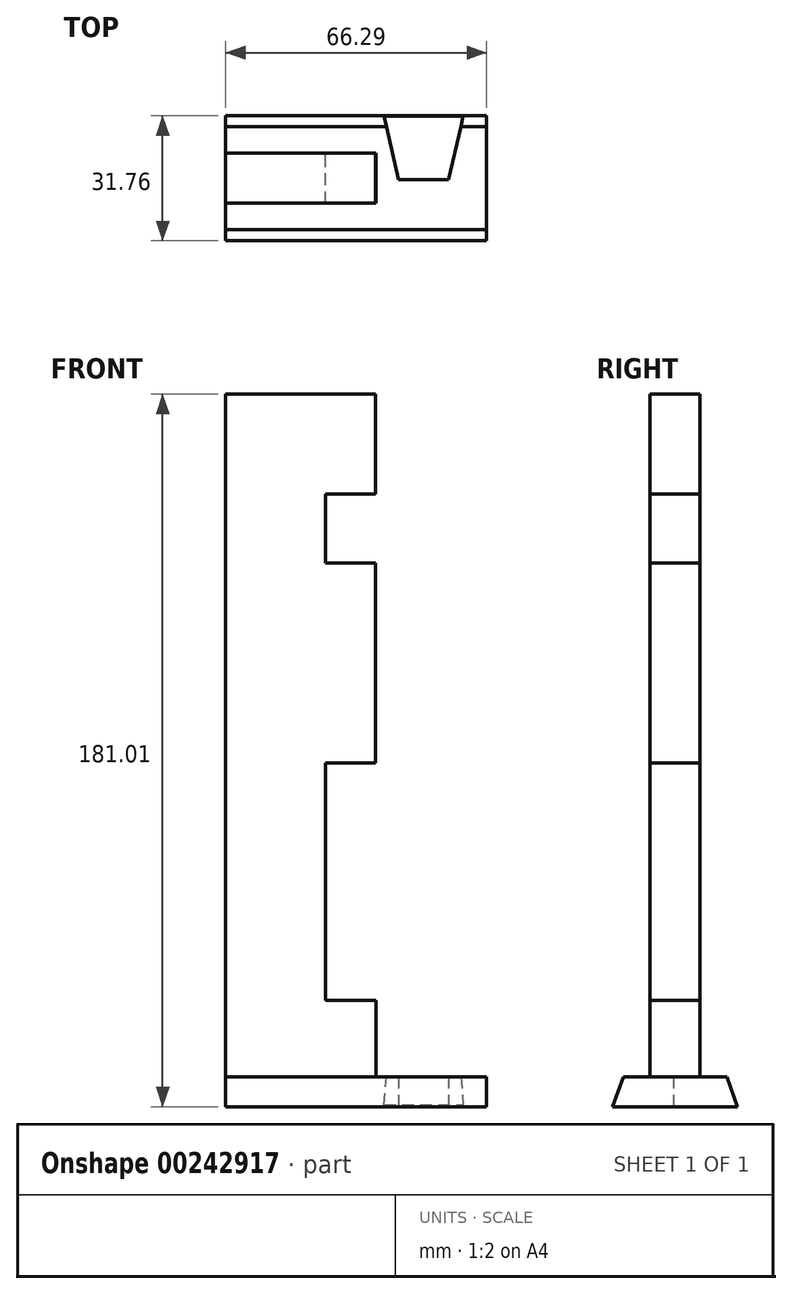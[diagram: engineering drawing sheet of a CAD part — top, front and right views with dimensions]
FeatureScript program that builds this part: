
annotation { "Feature Type Name" : "Feature", "Feature Type Description" : "" }
export const myFeature = defineFeature(function(context is Context, id is Id, definition is map)
    precondition{}
    {
        {
            var Q0;
            Q0=qCreatedBy(makeId("Front.planeOp"),FACE);
            var sketch = newSketch(context, id + "F0", { "sketchPlane" : qUnion([Q0])});
            skLineSegment(sketch, "E0", {"start": v(0, 0) * mm, "end": v(0, 173.39) * mm});
            skLineSegment(sketch, "E1", {"start": v(0, 173.39) * mm, "end": v(38.1, 173.39) * mm});
            skLineSegment(sketch, "E2", {"start": v(38.1, 173.39) * mm, "end": v(38.1, 147.99) * mm});
            skLineSegment(sketch, "E3", {"start": v(38.1, 147.99) * mm, "end": v(25.4, 147.99) * mm});
            skLineSegment(sketch, "E4", {"start": v(25.4, 147.99) * mm, "end": v(25.4, 130.53) * mm});
            skLineSegment(sketch, "E5", {"start": v(25.4, 130.53) * mm, "end": v(38.1, 130.53) * mm});
            skLineSegment(sketch, "E6", {"start": v(38.1, 130.53) * mm, "end": v(38.1, 79.73) * mm});
            skLineSegment(sketch, "E7", {"start": v(38.1, 79.73) * mm, "end": v(25.4, 79.73) * mm});
            skLineSegment(sketch, "E8", {"start": v(25.4, 79.73) * mm, "end": v(25.4, 19.4) * mm});
            skLineSegment(sketch, "E9", {"start": v(25.4, 19.4) * mm, "end": v(38.1, 19.4) * mm});
            skLineSegment(sketch, "E10", {"start": v(38.1, 19.4) * mm, "end": v(38.1, 0) * mm});
            skLineSegment(sketch, "E11", {"start": v(38.1, 0) * mm, "end": v(0, 0) * mm});
            skSolve(sketch);
        }
        {
            var Q0;
            Q0=makeQuery(id+"F0.imprint","IMPRINT",FACE,{"disambiguationData":[TD([[makeQuery(id+"F0.imprint","IMPRINT",EDGE,{"derivedFrom":sQuery(id+"F0.wireOp",EDGE,"E0")}),-1.0]])]});
            extrude(context, id + "F1", {"entities" : qUnion([Q0]), "depth" : 12.7 * mm});
        }
        {
            var Q0;
            Q0=makeQuery(id+"F1.opExtrude","SWEPT_FACE",FACE,{"disambiguationData":[OSD([sQuery(id+"F0.wireOp",EDGE,"E10")])]});
            var sketch = newSketch(context, id + "F2", { "sketchPlane" : qUnion([Q0])});
            skLineSegment(sketch, "E12.bottom", {"start": v(0, 0) * mm, "end": v(-12.7, 0) * mm});
            skLineSegment(sketch, "E12.top", {"start": v(0, -7.62) * mm, "end": v(-12.7, -7.62) * mm});
            skLineSegment(sketch, "E12.left", {"start": v(0, 0) * mm, "end": v(0, -7.62) * mm});
            skLineSegment(sketch, "E12.right", {"start": v(-12.7, 0) * mm, "end": v(-12.7, -7.62) * mm});
            skLineSegment(sketch, "E13", {"start": v(-12.7, -7.62) * mm, "end": v(-9.93, 0) * mm});
            skLineSegment(sketch, "E14", {"start": v(-9.93, 0) * mm, "end": v(-2.77, 0) * mm});
            skLineSegment(sketch, "E15", {"start": v(-2.77, 0) * mm, "end": v(0, -7.62) * mm});
            skSolve(sketch);
        }
        {
            var Q0;
            Q0=makeQuery(id+"F2.imprint","IMPRINT",FACE,{"disambiguationData":[TD([[makeQuery(id+"F2.imprint","IMPRINT",EDGE,{"derivedFrom":sQuery(id+"F2.wireOp",EDGE,"E12.top")}),-1.0]])]});
            extrude(context, id + "F3", {"entities" : qUnion([Q0]), "operationType" : NewBodyOperationType.ADD, "oppositeDirection" : true, "depth" : 38.1 * mm});
        }
        {
            var Q0;
            Q0=makeQuery(id+"F3.boolean.opBoolean","MERGE",FACE,{"derivedFrom":[makeQuery(id+"F1.opExtrude","SWEPT_FACE",FACE,{"disambiguationData":[OSD([sQuery(id+"F0.wireOp",EDGE,"E0")])]}),makeQuery(id+"F3.opExtrude","CAP_FACE",FACE,{"disambiguationData":[OSD([sQuery(id+"F2.wireOp",EDGE,"E12.top"),sQuery(id+"F2.wireOp",EDGE,"E13"),sQuery(id+"F2.wireOp",EDGE,"E14"),sQuery(id+"F2.wireOp",EDGE,"E15")])],"isStart":false})]});
            var sketch = newSketch(context, id + "F4", { "sketchPlane" : qUnion([Q0])});
            skLineSegment(sketch, "E16.bottom", {"start": v(0, 0) * mm, "end": v(14.78, 0) * mm});
            skLineSegment(sketch, "E16.top", {"start": v(0, -8.84) * mm, "end": v(14.78, -8.84) * mm});
            skLineSegment(sketch, "E16.left", {"start": v(0, 0) * mm, "end": v(0, -8.84) * mm});
            skLineSegment(sketch, "E16.right", {"start": v(14.78, 0) * mm, "end": v(14.78, -8.84) * mm});
            skSolve(sketch);
        }
        {
            var Q0;
            Q0=qSketchRegion(id+"F4",true);
            extrude(context, id + "F5", {"entities" : qUnion([Q0]), "operationType" : NewBodyOperationType.REMOVE, "oppositeDirection" : true, "depth" : 3.17 * mm});
        }
        {
            var Q0;
            Q0=makeQuery(id+"F3.boolean.opBoolean","MERGE",FACE,{"derivedFrom":[makeQuery(id+"F1.opExtrude","SWEPT_FACE",FACE,{"disambiguationData":[OSD([sQuery(id+"F0.wireOp",EDGE,"E10")])]}),makeQuery(id+"F3.opExtrude","CAP_FACE",FACE,{"disambiguationData":[OSD([sQuery(id+"F2.wireOp",EDGE,"E12.top"),sQuery(id+"F2.wireOp",EDGE,"E13"),sQuery(id+"F2.wireOp",EDGE,"E14"),sQuery(id+"F2.wireOp",EDGE,"E15")])],"isStart":true})]});
            var sketch = newSketch(context, id + "F6", { "sketchPlane" : qUnion([Q0])});
            skLineSegment(sketch, "E17", {"start": v(0, 0) * mm, "end": v(-22.22, 0) * mm});
            skLineSegment(sketch, "E18", {"start": v(-22.22, 0) * mm, "end": v(0, 0) * mm});
            skLineSegment(sketch, "E19", {"start": v(9.53, 0) * mm, "end": v(0, 0) * mm});
            skPoint(sketch, "E20.startSnap0", {"position": v(-6.35, -7.62) * mm});
            skLineSegment(sketch, "E21", {"start": v(-22.22, 0) * mm, "end": v(-22.22, -7.62) * mm});
            skLineSegment(sketch, "E22", {"start": v(9.53, 0) * mm, "end": v(9.53, -7.62) * mm});
            skLineSegment(sketch, "E23", {"start": v(-22.22, -7.62) * mm, "end": v(9.53, -7.62) * mm});
            skLineSegment(sketch, "E24", {"start": v(-22.22, -7.62) * mm, "end": v(-19.45, 0) * mm});
            skLineSegment(sketch, "E25", {"start": v(9.53, -7.62) * mm, "end": v(6.75, 0) * mm});
            skLineSegment(sketch, "E26", {"start": v(-22.22, 0) * mm, "end": v(9.53, 0) * mm});
            skLineSegment(sketch, "E27.bottom", {"start": v(-12.7, 0) * mm, "end": v(0, 0) * mm});
            skLineSegment(sketch, "E27.top", {"start": v(-12.7, 19.4) * mm, "end": v(0, 19.4) * mm});
            skLineSegment(sketch, "E27.left", {"start": v(-12.7, 0) * mm, "end": v(-12.7, 19.4) * mm});
            skLineSegment(sketch, "E27.right", {"start": v(0, 0) * mm, "end": v(0, 19.4) * mm});
            skSolve(sketch);
        }
        {
            var Q0;
            {var subQ4=sQuery(id+"F6.wireOp",EDGE,"E24");Q0=makeQuery(id+"F6.imprint","IMPRINT",FACE,{"disambiguationData":[TD([[makeQuery(id+"F6.imprint","IMPRINT",EDGE,{"derivedFrom":subQ4}),-1.0]])]});}
            var Q1;
            {var subQ2=makeQuery(id+"F3.opExtrude","CAP_EDGE",EDGE,{"disambiguationData":[OSD([sQuery(id+"F2.wireOp",EDGE,"E13")])],"isStart":true});Q1=makeQuery(id+"F6.imprint","IMPRINT",FACE,{"disambiguationData":[TD([[makeQuery(id+"F6.imprint","IMPRINT",EDGE,{"derivedFrom":subQ2}),-1.0]])]});}
            var Q2;
            Q2=makeQuery(id+"F6.imprint","IMPRINT",FACE,{"disambiguationData":[TD([[makeQuery(id+"F6.imprint","IMPRINT",EDGE,{"derivedFrom":sQuery(id+"F6.wireOp",EDGE,"E27.top")}),-1.0]])]});
            var Q3;
            {var subQ4=sQuery(id+"F6.wireOp",EDGE,"E25");Q3=makeQuery(id+"F6.imprint","IMPRINT",FACE,{"disambiguationData":[TD([[makeQuery(id+"F6.imprint","IMPRINT",EDGE,{"derivedFrom":subQ4}),1.0]])]});}
            extrude(context, id + "F7", {"entities" : qUnion([Q0, Q1, Q2, Q3]), "operationType" : NewBodyOperationType.ADD, "depth" : 66.67 * mm});
        }
        {
            var Q0;
            Q0=makeQuery(id+"F7.opExtrude","CAP_FACE",FACE,{"disambiguationData":[OSD([sQuery(id+"F6.wireOp",EDGE,"E23"),sQuery(id+"F6.wireOp",EDGE,"E24"),sQuery(id+"F6.wireOp",EDGE,"E25"),sQuery(id+"F6.wireOp",EDGE,"E26"),sQuery(id+"F6.wireOp",EDGE,"E27.top"),sQuery(id+"F6.wireOp",EDGE,"E27.left"),sQuery(id+"F6.wireOp",EDGE,"E27.right")])],"isStart":false});
            var sketch = newSketch(context, id + "F8", { "sketchPlane" : qUnion([Q0])});
            skLineSegment(sketch, "E28.bottom", {"start": v(0, 0) * mm, "end": v(-12.7, 0) * mm});
            skLineSegment(sketch, "E28.top", {"start": v(0, 19.4) * mm, "end": v(-12.7, 19.4) * mm});
            skLineSegment(sketch, "E28.left", {"start": v(0, 0) * mm, "end": v(0, 19.4) * mm});
            skLineSegment(sketch, "E28.right", {"start": v(-12.7, 0) * mm, "end": v(-12.7, 19.4) * mm});
            skSolve(sketch);
        }
        {
            var Q0;
            Q0=makeQuery(id+"F8.imprint","IMPRINT",FACE,{"disambiguationData":[TD([[makeQuery(id+"F8.imprint","IMPRINT",EDGE,{"derivedFrom":sQuery(id+"F8.wireOp",EDGE,"E28.bottom")}),-1.0]])]});
            extrude(context, id + "F9", {"entities" : qUnion([Q0]), "operationType" : NewBodyOperationType.REMOVE, "oppositeDirection" : true, "depth" : 66.55 * mm});
        }
        {
            var Q0;
            {var subQ4=sQuery(id+"F6.wireOp",EDGE,"E25");Q0=makeQuery(id+"F6.imprint","IMPRINT",FACE,{"disambiguationData":[TD([[makeQuery(id+"F6.imprint","IMPRINT",EDGE,{"derivedFrom":subQ4}),1.0]])]});}
            var Q1;
            {var subQ4=sQuery(id+"F6.wireOp",EDGE,"E24");Q1=makeQuery(id+"F6.imprint","IMPRINT",FACE,{"disambiguationData":[TD([[makeQuery(id+"F6.imprint","IMPRINT",EDGE,{"derivedFrom":subQ4}),-1.0]])]});}
            extrude(context, id + "F10", {"entities" : qUnion([Q0, Q1]), "operationType" : NewBodyOperationType.ADD, "oppositeDirection" : true, "depth" : 34.92 * mm});
        }
        {
            var Q0;
            {var subQ0=sQuery(id+"F6.wireOp",EDGE,"E23");Q0=makeQuery(id+"F10.boolean.opBoolean","MERGE",FACE,{"derivedFrom":[makeQuery(id+"F7.boolean.opBoolean","MERGE",FACE,{"derivedFrom":[makeQuery(id+"F3.opExtrude","SWEPT_FACE",FACE,{"disambiguationData":[OSD([sQuery(id+"F2.wireOp",EDGE,"E12.top")])]}),makeQuery(id+"F7.opExtrude","SWEPT_FACE",FACE,{"disambiguationData":[OSD([subQ0])]})]}),makeQuery(id+"F10.opExtrude","SWEPT_FACE",FACE,{"disambiguationData":[OSD([subQ0]),TDD([makeQuery(id+"F6.imprint","IMPRINT",EDGE,{"disambiguationData":[TD([[makeQuery(id+"F6.imprint","INTERSECT",VERTEX,{"derivedFrom":[makeQuery(id+"F3.opExtrude","CAP_EDGE",EDGE,{"disambiguationData":[OSD([sQuery(id+"F2.wireOp",EDGE,"E13")])],"isStart":true}),subQ0]}),1.0],[makeQuery(id+"F6.imprint","INTERSECT",VERTEX,{"derivedFrom":[sQuery(id+"F6.wireOp",EDGE,"E21"),subQ0,sQuery(id+"F6.wireOp",EDGE,"E24")]}),-1.0]])],"derivedFrom":subQ0})])]}),makeQuery(id+"F10.opExtrude","SWEPT_FACE",FACE,{"disambiguationData":[OSD([subQ0]),TDD([makeQuery(id+"F6.imprint","IMPRINT",EDGE,{"disambiguationData":[TD([[makeQuery(id+"F6.imprint","INTERSECT",VERTEX,{"derivedFrom":[makeQuery(id+"F3.opExtrude","CAP_EDGE",EDGE,{"disambiguationData":[OSD([sQuery(id+"F2.wireOp",EDGE,"E15")])],"isStart":true}),subQ0]}),-1.0],[makeQuery(id+"F6.imprint","INTERSECT",VERTEX,{"derivedFrom":[sQuery(id+"F6.wireOp",EDGE,"E22"),subQ0,sQuery(id+"F6.wireOp",EDGE,"E25")]}),1.0]])],"derivedFrom":subQ0})])]})]});}
            var sketch = newSketch(context, id + "F11", { "sketchPlane" : qUnion([Q0])});
            skLineSegment(sketch, "E29.bottom", {"start": v(3.18, 22.22) * mm, "end": v(69.85, 22.22) * mm});
            skLineSegment(sketch, "E29.top", {"start": v(3.18, -9.53) * mm, "end": v(69.85, -9.53) * mm});
            skLineSegment(sketch, "E29.left", {"start": v(3.18, 22.22) * mm, "end": v(3.18, -9.53) * mm});
            skLineSegment(sketch, "E29.right", {"start": v(69.85, 22.22) * mm, "end": v(69.85, -9.53) * mm});
            skLineSegment(sketch, "E30", {"start": v(69.85, 22.22) * mm, "end": v(104.78, 22.22) * mm});
            skLineSegment(sketch, "E31", {"start": v(69.85, -9.53) * mm, "end": v(104.78, -9.53) * mm});
            skLineSegment(sketch, "E32", {"start": v(104.78, -9.53) * mm, "end": v(104.78, 22.22) * mm});
            skSolve(sketch);
        }
        {
            var Q0;
            Q0=makeQuery(id+"F11.imprint","IMPRINT",FACE,{"disambiguationData":[TD([[makeQuery(id+"F11.imprint","IMPRINT",EDGE,{"derivedFrom":sQuery(id+"F11.wireOp",EDGE,"E29.right")}),1.0]])]});
            extrude(context, id + "F12", {"entities" : qUnion([Q0]), "operationType" : NewBodyOperationType.REMOVE, "oppositeDirection" : true, "depth" : 25.4 * mm});
        }
        {
            var Q0;
            {var subQ0=sQuery(id+"F6.wireOp",EDGE,"E23");Q0=makeQuery(id+"F10.boolean.opBoolean","MERGE",FACE,{"derivedFrom":[makeQuery(id+"F7.boolean.opBoolean","MERGE",FACE,{"derivedFrom":[makeQuery(id+"F3.opExtrude","SWEPT_FACE",FACE,{"disambiguationData":[OSD([sQuery(id+"F2.wireOp",EDGE,"E12.top")])]}),makeQuery(id+"F7.opExtrude","SWEPT_FACE",FACE,{"disambiguationData":[OSD([subQ0])]})]}),makeQuery(id+"F10.opExtrude","SWEPT_FACE",FACE,{"disambiguationData":[OSD([subQ0]),TDD([makeQuery(id+"F6.imprint","IMPRINT",EDGE,{"disambiguationData":[TD([[makeQuery(id+"F6.imprint","INTERSECT",VERTEX,{"derivedFrom":[makeQuery(id+"F3.opExtrude","CAP_EDGE",EDGE,{"disambiguationData":[OSD([sQuery(id+"F2.wireOp",EDGE,"E13")])],"isStart":true}),subQ0]}),1.0],[makeQuery(id+"F6.imprint","INTERSECT",VERTEX,{"derivedFrom":[sQuery(id+"F6.wireOp",EDGE,"E21"),subQ0,sQuery(id+"F6.wireOp",EDGE,"E24")]}),-1.0]])],"derivedFrom":subQ0})])]}),makeQuery(id+"F10.opExtrude","SWEPT_FACE",FACE,{"disambiguationData":[OSD([subQ0]),TDD([makeQuery(id+"F6.imprint","IMPRINT",EDGE,{"disambiguationData":[TD([[makeQuery(id+"F6.imprint","INTERSECT",VERTEX,{"derivedFrom":[makeQuery(id+"F3.opExtrude","CAP_EDGE",EDGE,{"disambiguationData":[OSD([sQuery(id+"F2.wireOp",EDGE,"E15")])],"isStart":true}),subQ0]}),-1.0],[makeQuery(id+"F6.imprint","INTERSECT",VERTEX,{"derivedFrom":[sQuery(id+"F6.wireOp",EDGE,"E22"),subQ0,sQuery(id+"F6.wireOp",EDGE,"E25")]}),1.0]])],"derivedFrom":subQ0})])]})]});}
            var sketch = newSketch(context, id + "F13", { "sketchPlane" : qUnion([Q0])});
            skLineSegment(sketch, "E33.bottom", {"start": v(69.85, -9.53) * mm, "end": v(66.68, -9.53) * mm});
            skLineSegment(sketch, "E33.top", {"start": v(69.85, 22.22) * mm, "end": v(66.68, 22.22) * mm});
            skLineSegment(sketch, "E33.left", {"start": v(69.85, -9.53) * mm, "end": v(69.85, 22.22) * mm});
            skLineSegment(sketch, "E33.right", {"start": v(66.68, -9.53) * mm, "end": v(66.68, 22.22) * mm});
            skSolve(sketch);
        }
        {
            var Q0;
            Q0=makeQuery(id+"F13.imprint","IMPRINT",FACE,{"disambiguationData":[TD([[makeQuery(id+"F13.imprint","IMPRINT",EDGE,{"derivedFrom":sQuery(id+"F13.wireOp",EDGE,"E33.bottom")}),-1.0]])]});
            extrude(context, id + "F14", {"entities" : qUnion([Q0]), "operationType" : NewBodyOperationType.REMOVE, "oppositeDirection" : true, "depth" : 25.4 * mm});
        }
        {
            var Q0;
            {var subQ0=sQuery(id+"F6.wireOp",EDGE,"E27.bottom");var subQ1=sQuery(id+"F6.wireOp",EDGE,"E26");var subQ2=sQuery(id+"F6.wireOp",EDGE,"E23");Q0=makeQuery(id+"F10.boolean.opBoolean","MERGE",FACE,{"derivedFrom":[makeQuery(id+"F5.boolean.opBoolean","COPY",FACE,{"derivedFrom":makeQuery(id+"F5.opExtrude","CAP_FACE",FACE,{"disambiguationData":[OSD([sQuery(id+"F4.wireOp",EDGE,"E16.bottom"),sQuery(id+"F4.wireOp",EDGE,"E16.top"),sQuery(id+"F4.wireOp",EDGE,"E16.left"),sQuery(id+"F4.wireOp",EDGE,"E16.right")])],"isStart":false})}),makeQuery(id+"F10.opExtrude","CAP_FACE",FACE,{"disambiguationData":[OSD([sQuery(id+"F2.wireOp",EDGE,"E13"),subQ2,sQuery(id+"F6.wireOp",EDGE,"E24"),subQ1,subQ0])],"isStart":false}),makeQuery(id+"F10.opExtrude","CAP_FACE",FACE,{"disambiguationData":[OSD([sQuery(id+"F2.wireOp",EDGE,"E15"),subQ2,sQuery(id+"F6.wireOp",EDGE,"E25"),subQ1,subQ0])],"isStart":false})]});}
            extrude(context, id + "F15", {"entities" : qUnion([Q0]), "operationType" : NewBodyOperationType.ADD, "depth" : 3.17 * mm});
        }
        {
            var Q0;
            {var subQ0=sQuery(id+"F6.wireOp",EDGE,"E27.bottom");var subQ1=sQuery(id+"F6.wireOp",EDGE,"E26");var subQ3=makeQuery(id+"F6.imprint","IMPRINT",EDGE,{"disambiguationData":[TD([[makeQuery(id+"F6.imprint","INTERSECT",VERTEX,{"derivedFrom":[sQuery(id+"F6.wireOp",EDGE,"E25"),subQ1]}),1.0]])],"derivedFrom":subQ1});var subQ5=makeQuery(id+"F6.imprint","IMPRINT",EDGE,{"disambiguationData":[TD([[makeQuery(id+"F6.imprint","INTERSECT",VERTEX,{"derivedFrom":[sQuery(id+"F6.wireOp",EDGE,"E24"),subQ1]}),-1.0]])],"derivedFrom":subQ1});Q0=makeQuery(id+"F15.boolean.opBoolean","MERGE",FACE,{"derivedFrom":[makeQuery(id+"F10.boolean.opBoolean","MERGE",FACE,{"derivedFrom":[makeQuery(id+"F9.boolean.opBoolean","MERGE",FACE,{"derivedFrom":[makeQuery(id+"F7.opExtrude","SWEPT_FACE",FACE,{"disambiguationData":[OSD([subQ1]),TDD([subQ5])]}),makeQuery(id+"F7.opExtrude","SWEPT_FACE",FACE,{"disambiguationData":[OSD([subQ1]),TDD([subQ3])]}),makeQuery(id+"F9.opExtrude","SWEPT_FACE",FACE,{"disambiguationData":[OSD([sQuery(id+"F8.wireOp",EDGE,"E28.bottom")])]})]}),makeQuery(id+"F10.opExtrude","SWEPT_FACE",FACE,{"disambiguationData":[OSD([subQ1,subQ0]),TDD([subQ5,makeQuery(id+"F6.imprint","IMPRINT",EDGE,{"disambiguationData":[TD([[makeQuery(id+"F6.imprint","INTERSECT",VERTEX,{"derivedFrom":[makeQuery(id+"F3.opExtrude","CAP_EDGE",EDGE,{"disambiguationData":[OSD([sQuery(id+"F2.wireOp",EDGE,"E13")])],"isStart":true}),subQ0]}),1.0]])],"derivedFrom":subQ0})])]}),makeQuery(id+"F10.opExtrude","SWEPT_FACE",FACE,{"disambiguationData":[OSD([subQ1,subQ0]),TDD([subQ3,makeQuery(id+"F6.imprint","IMPRINT",EDGE,{"disambiguationData":[TD([[makeQuery(id+"F6.imprint","INTERSECT",VERTEX,{"derivedFrom":[makeQuery(id+"F3.opExtrude","CAP_EDGE",EDGE,{"disambiguationData":[OSD([sQuery(id+"F2.wireOp",EDGE,"E15")])],"isStart":true}),subQ0]}),-1.0]])],"derivedFrom":subQ0})])]})]}),makeQuery(id+"F15.opExtrude","SWEPT_FACE",FACE,{"disambiguationData":[OSD([sQuery(id+"F4.wireOp",EDGE,"E16.bottom"),subQ1,subQ0])]})]});}
            var sketch = newSketch(context, id + "F16", { "sketchPlane" : qUnion([Q0])});
            skLineSegment(sketch, "E34.bottom", {"start": v(40.2, -9.38) * mm, "end": v(60.33, -9.38) * mm});
            skLineSegment(sketch, "E34.top", {"start": v(40.2, 22.88) * mm, "end": v(60.33, 22.88) * mm});
            skLineSegment(sketch, "E34.left", {"start": v(40.2, -9.38) * mm, "end": v(40.2, 22.88) * mm});
            skLineSegment(sketch, "E34.right", {"start": v(60.33, -9.38) * mm, "end": v(60.33, 22.88) * mm});
            skLineSegment(sketch, "E35", {"start": v(40.2, 6.75) * mm, "end": v(60.33, 6.75) * mm});
            skLineSegment(sketch, "E36", {"start": v(60.33, 22.88) * mm, "end": v(56.6, 6.75) * mm});
            skLineSegment(sketch, "E37", {"start": v(56.6, 6.75) * mm, "end": v(60.33, -9.38) * mm});
            skLineSegment(sketch, "E38", {"start": v(40.2, -9.38) * mm, "end": v(43.92, 6.75) * mm});
            skLineSegment(sketch, "E39", {"start": v(43.92, 6.75) * mm, "end": v(40.2, 22.88) * mm});
            skSolve(sketch);
        }
        {
            var Q0;
            Q0=makeQuery(id+"F16.imprint","IMPRINT",FACE,{"disambiguationData":[TD([[makeQuery(id+"F16.imprint","IMPRINT",EDGE,{"derivedFrom":sQuery(id+"F16.wireOp",EDGE,"E34.bottom")}),1.0]])]});
            var Q1;
            Q1=makeQuery(id+"F16.imprint","IMPRINT",FACE,{"disambiguationData":[TD([[makeQuery(id+"F16.imprint","IMPRINT",EDGE,{"derivedFrom":sQuery(id+"F16.wireOp",EDGE,"E34.top")}),-1.0]])]});
            extrude(context, id + "F17", {"entities" : qUnion([Q0, Q1]), "operationType" : NewBodyOperationType.REMOVE, "oppositeDirection" : true, "depth" : 8.13 * mm});
        }
        {
            var Q0;
            Q0=makeQuery(id+"F14.boolean.opBoolean","COPY",FACE,{"derivedFrom":makeQuery(id+"F14.opExtrude","SWEPT_FACE",FACE,{"disambiguationData":[OSD([sQuery(id+"F13.wireOp",EDGE,"E33.right")])]})});
            var sketch = newSketch(context, id + "F18", { "sketchPlane" : qUnion([Q0])});
            skLineSegment(sketch, "E40", {"start": v(-22.22, -7.62) * mm, "end": v(-19.45, 0) * mm});
            skLineSegment(sketch, "E41", {"start": v(-19.45, 0) * mm, "end": v(6.75, 0) * mm});
            skLineSegment(sketch, "E42", {"start": v(6.75, 0) * mm, "end": v(9.53, -7.62) * mm});
            skLineSegment(sketch, "E43", {"start": v(9.53, -7.62) * mm, "end": v(-22.22, -7.62) * mm});
            skSolve(sketch);
        }
        {
            var Q0;
            Q0 = qSketchRegion(id + "F18", true);
            extrude(context, id + "F19", {"entities" : qUnion([Q0]), "operationType" : NewBodyOperationType.REMOVE, "oppositeDirection" : true, "depth" : 0.38 * mm});
        }
    });
